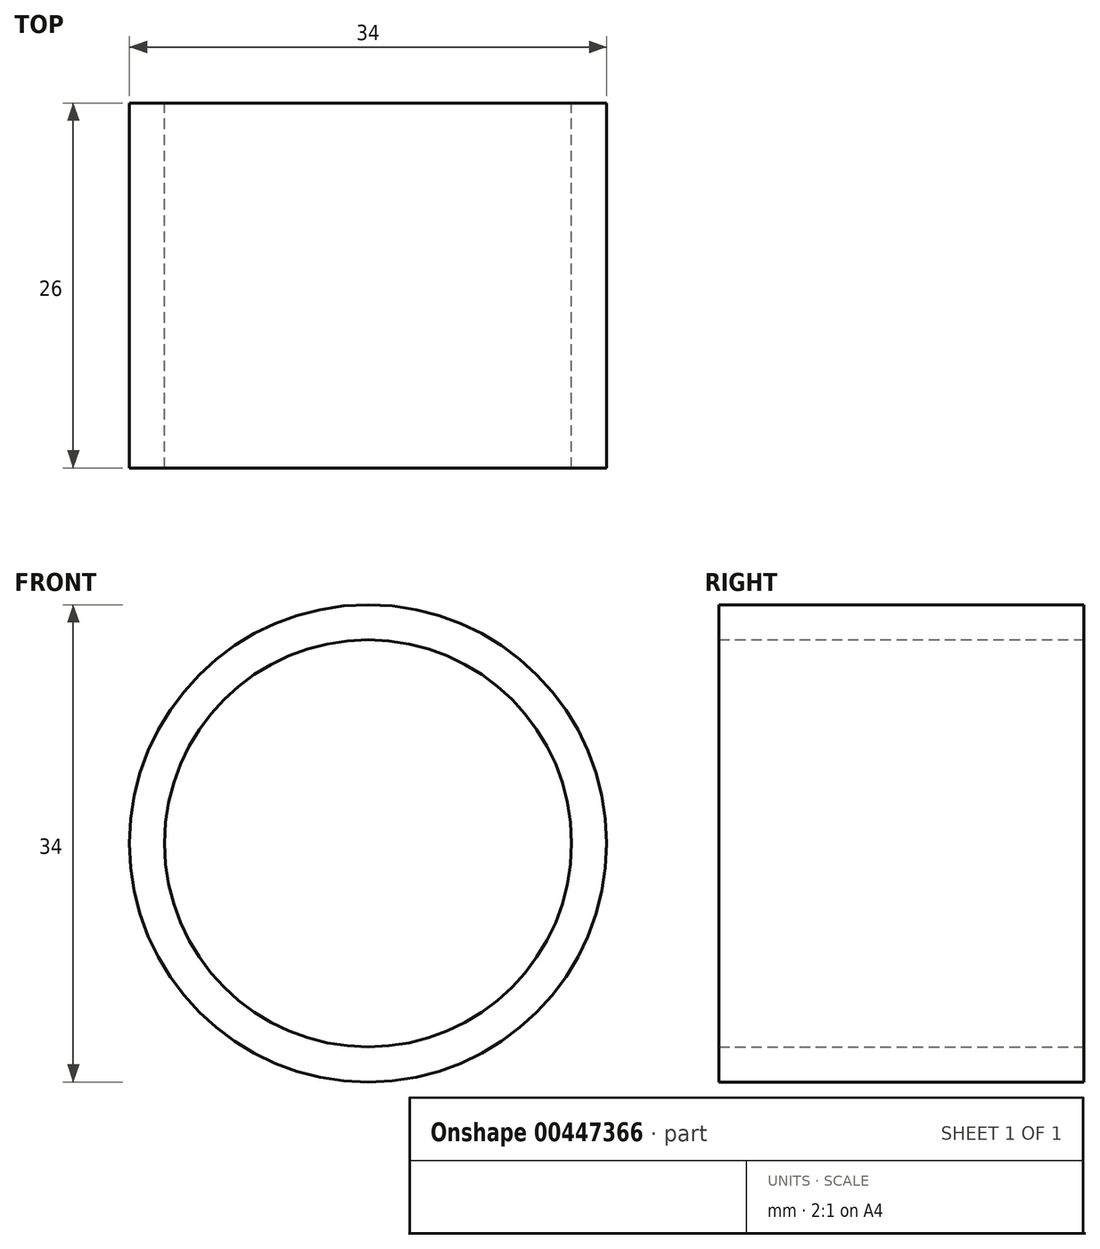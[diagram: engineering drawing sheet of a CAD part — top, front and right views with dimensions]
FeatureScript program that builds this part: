
annotation { "Feature Type Name" : "Feature", "Feature Type Description" : "" }
export const myFeature = defineFeature(function(context is Context, id is Id, definition is map)
    precondition{}
    {
        {
            var Q0;
            Q0=qCreatedBy(makeId("Front.planeOp"),FACE);
            var sketch = newSketch(context, id + "F0", { "sketchPlane" : qUnion([Q0])});
            skCircle(sketch, "E0", {"center": v(0, 0) * mm, "radius": 17 * mm});
            skCircle(sketch, "E1", {"center": v(0, 0) * mm, "radius": 14.5 * mm});
            skSolve(sketch);
        }
        {
            var Q0;
            Q0=makeQuery(id+"F0.imprint","IMPRINT",FACE,{"disambiguationData":[TD([[makeQuery(id+"F0.imprint","IMPRINT",EDGE,{"derivedFrom":sQuery(id+"F0.wireOp",EDGE,"E0")}),1.0]])]});
            extrude(context, id + "F1", {"entities" : qUnion([Q0]), "depth" : 26 * mm});
        }
    });
